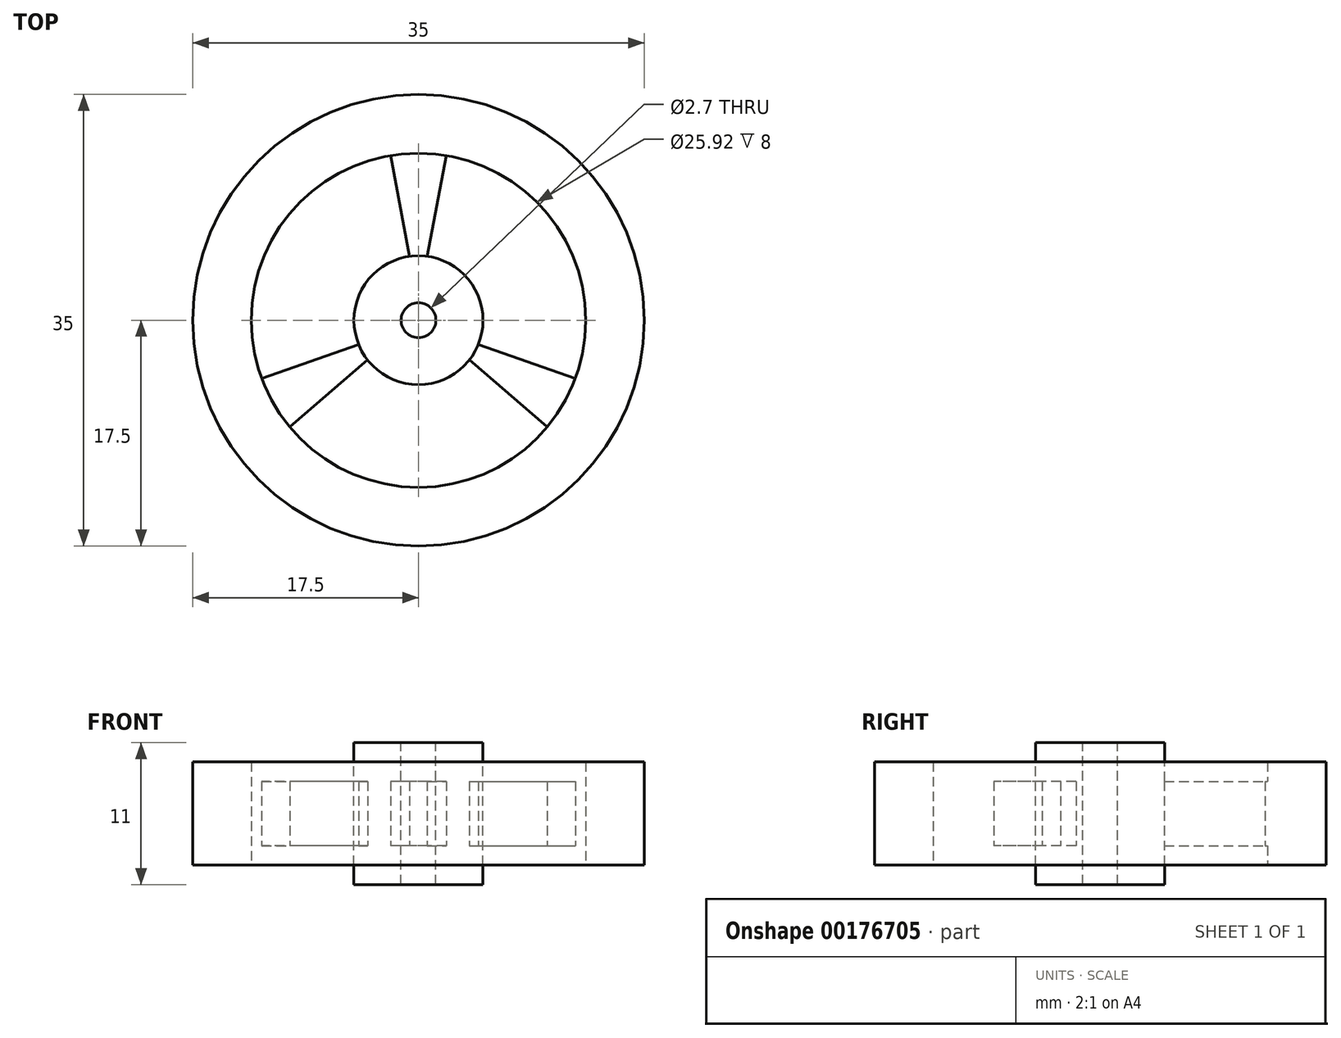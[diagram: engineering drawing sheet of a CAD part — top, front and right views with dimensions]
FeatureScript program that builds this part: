
annotation { "Feature Type Name" : "Feature", "Feature Type Description" : "" }
export const myFeature = defineFeature(function(context is Context, id is Id, definition is map)
    precondition{}
    {
        {
            var Q0;
            Q0=qCreatedBy(makeId("Top.planeOp"),FACE);
            var sketch = newSketch(context, id + "F0", { "sketchPlane" : qUnion([Q0])});
            skCircle(sketch, "E0", {"center": v(0, 0) * mm, "radius": 17.5 * mm});
            skCircle(sketch, "E1", {"center": v(0, 0) * mm, "radius": 12.96 * mm});
            skCircle(sketch, "E2", {"center": v(0, 0) * mm, "radius": 1.35 * mm});
            skLineSegment(sketch, "E3", {"start": v(0, 1.35) * mm, "end": v(0, 12.96) * mm});
            skLineSegment(sketch, "E4", {"start": v(0, 1.35) * mm, "end": v(2.17, 12.78) * mm});
            skLineSegment(sketch, "E5.MirrorCS", {"start": v(0, 1.35) * mm, "end": v(-2.17, 12.78) * mm});
            skCircle(sketch, "E6", {"center": v(0, 0) * mm, "radius": 5 * mm});
            skLineSegment(sketch, "E7.1.0", {"start": v(-1.17, -0.67) * mm, "end": v(-12.15, -4.5) * mm});
            skLineSegment(sketch, "E7.1.1", {"start": v(-1.17, -0.67) * mm, "end": v(-9.98, -8.27) * mm});
            skLineSegment(sketch, "E7.2.0", {"start": v(1.17, -0.67) * mm, "end": v(9.98, -8.27) * mm});
            skLineSegment(sketch, "E7.2.1", {"start": v(1.17, -0.68) * mm, "end": v(12.15, -4.5) * mm});
            skSolve(sketch);
        }
        {
            var Q0;
            {var subQ0=sQuery(id+"F0.wireOp",EDGE,"E5.MirrorCS");var subQ5=sQuery(id+"F0.wireOp",EDGE,"E6");var subQ6=makeQuery(id+"F0.imprint","INTERSECT",VERTEX,{"derivedFrom":[subQ0,subQ5]});Q0=makeQuery(id+"F0.imprint","IMPRINT",FACE,{"disambiguationData":[TD([[makeQuery(id+"F0.imprint","IMPRINT",EDGE,{"disambiguationData":[TD([[subQ6,-1.0]])],"derivedFrom":subQ5}),1.0]])]});}
            var Q1;
            {var subQ0=sQuery(id+"F0.wireOp",EDGE,"E7.1.0");var subQ1=sQuery(id+"F0.wireOp",EDGE,"E6");var subQ2=makeQuery(id+"F0.imprint","INTERSECT",VERTEX,{"derivedFrom":[subQ1,subQ0]});Q1=makeQuery(id+"F0.imprint","IMPRINT",FACE,{"disambiguationData":[TD([[makeQuery(id+"F0.imprint","IMPRINT",EDGE,{"disambiguationData":[TD([[subQ2,-1.0]])],"derivedFrom":subQ1}),1.0]])]});}
            var Q2;
            {var subQ0=sQuery(id+"F0.wireOp",EDGE,"E7.1.1");var subQ5=sQuery(id+"F0.wireOp",EDGE,"E6");var subQ6=makeQuery(id+"F0.imprint","INTERSECT",VERTEX,{"derivedFrom":[subQ5,subQ0]});Q2=makeQuery(id+"F0.imprint","IMPRINT",FACE,{"disambiguationData":[TD([[makeQuery(id+"F0.imprint","IMPRINT",EDGE,{"disambiguationData":[TD([[subQ6,-1.0]])],"derivedFrom":subQ5}),1.0]])]});}
            var Q3;
            {var subQ0=sQuery(id+"F0.wireOp",EDGE,"E4");var subQ5=sQuery(id+"F0.wireOp",EDGE,"E6");var subQ7=makeQuery(id+"F0.imprint","INTERSECT",VERTEX,{"derivedFrom":[subQ0,subQ5]});Q3=makeQuery(id+"F0.imprint","IMPRINT",FACE,{"disambiguationData":[TD([[makeQuery(id+"F0.imprint","IMPRINT",EDGE,{"disambiguationData":[TD([[subQ7,1.0]])],"derivedFrom":subQ5}),1.0]])]});}
            var Q4;
            {var subQ0=sQuery(id+"F0.wireOp",EDGE,"E7.2.0");var subQ1=sQuery(id+"F0.wireOp",EDGE,"E6");var subQ2=makeQuery(id+"F0.imprint","INTERSECT",VERTEX,{"derivedFrom":[subQ1,subQ0]});Q4=makeQuery(id+"F0.imprint","IMPRINT",FACE,{"disambiguationData":[TD([[makeQuery(id+"F0.imprint","IMPRINT",EDGE,{"disambiguationData":[TD([[subQ2,-1.0]])],"derivedFrom":subQ1}),1.0]])]});}
            var Q5;
            {var subQ1=sQuery(id+"F0.wireOp",EDGE,"E3");var subQ3=sQuery(id+"F0.wireOp",EDGE,"E6");var subQ4=makeQuery(id+"F0.imprint","INTERSECT",VERTEX,{"derivedFrom":[subQ1,subQ3]});Q5=makeQuery(id+"F0.imprint","IMPRINT",FACE,{"disambiguationData":[TD([[makeQuery(id+"F0.imprint","IMPRINT",EDGE,{"disambiguationData":[TD([[subQ4,1.0]])],"derivedFrom":subQ3}),1.0]])]});}
            var Q6;
            {var subQ1=sQuery(id+"F0.wireOp",EDGE,"E3");var subQ3=sQuery(id+"F0.wireOp",EDGE,"E6");var subQ4=makeQuery(id+"F0.imprint","INTERSECT",VERTEX,{"derivedFrom":[subQ1,subQ3]});Q6=makeQuery(id+"F0.imprint","IMPRINT",FACE,{"disambiguationData":[TD([[makeQuery(id+"F0.imprint","IMPRINT",EDGE,{"disambiguationData":[TD([[subQ4,-1.0]])],"derivedFrom":subQ3}),1.0]])]});}
            extrude(context, id + "F1", {"entities" : qUnion([Q0, Q1, Q2, Q3, Q4, Q5, Q6]), "endBound" : BoundingType.SYMMETRIC, "oppositeDirection" : true, "depth" : 11 * mm});
        }
        {
            var Q0;
            {var subQ0=sQuery(id+"F0.wireOp",EDGE,"E3");var subQ1=sQuery(id+"F0.wireOp",EDGE,"E1");var subQ2=makeQuery(id+"F0.imprint","INTERSECT",VERTEX,{"derivedFrom":[subQ1,subQ0]});Q0=makeQuery(id+"F0.imprint","IMPRINT",FACE,{"disambiguationData":[TD([[makeQuery(id+"F0.imprint","IMPRINT",EDGE,{"disambiguationData":[TD([[subQ2,1.0]])],"derivedFrom":subQ1}),1.0]])]});}
            var Q1;
            {var subQ0=sQuery(id+"F0.wireOp",EDGE,"E3");var subQ1=sQuery(id+"F0.wireOp",EDGE,"E1");var subQ2=makeQuery(id+"F0.imprint","INTERSECT",VERTEX,{"derivedFrom":[subQ1,subQ0]});Q1=makeQuery(id+"F0.imprint","IMPRINT",FACE,{"disambiguationData":[TD([[makeQuery(id+"F0.imprint","IMPRINT",EDGE,{"disambiguationData":[TD([[subQ2,-1.0]])],"derivedFrom":subQ1}),1.0]])]});}
            var Q2;
            {var subQ0=sQuery(id+"F0.wireOp",EDGE,"E7.1.0");var subQ1=sQuery(id+"F0.wireOp",EDGE,"E1");var subQ2=makeQuery(id+"F0.imprint","INTERSECT",VERTEX,{"derivedFrom":[subQ1,subQ0]});Q2=makeQuery(id+"F0.imprint","IMPRINT",FACE,{"disambiguationData":[TD([[makeQuery(id+"F0.imprint","IMPRINT",EDGE,{"disambiguationData":[TD([[subQ2,-1.0]])],"derivedFrom":subQ1}),1.0]])]});}
            var Q3;
            {var subQ0=sQuery(id+"F0.wireOp",EDGE,"E7.2.0");var subQ1=sQuery(id+"F0.wireOp",EDGE,"E1");var subQ2=makeQuery(id+"F0.imprint","INTERSECT",VERTEX,{"derivedFrom":[subQ1,subQ0]});Q3=makeQuery(id+"F0.imprint","IMPRINT",FACE,{"disambiguationData":[TD([[makeQuery(id+"F0.imprint","IMPRINT",EDGE,{"disambiguationData":[TD([[subQ2,-1.0]])],"derivedFrom":subQ1}),1.0]])]});}
            extrude(context, id + "F2", {"entities" : qUnion([Q0, Q1, Q2, Q3]), "operationType" : NewBodyOperationType.ADD, "endBound" : BoundingType.SYMMETRIC, "depth" : 5 * mm});
        }
        {
            var Q0;
            Q0=makeQuery(id+"F0.imprint","IMPRINT",FACE,{"disambiguationData":[TD([[makeQuery(id+"F0.imprint","IMPRINT",EDGE,{"derivedFrom":sQuery(id+"F0.wireOp",EDGE,"E0")}),1.0]])]});
            extrude(context, id + "F3", {"entities" : qUnion([Q0]), "operationType" : NewBodyOperationType.ADD, "endBound" : BoundingType.SYMMETRIC, "depth" : 8 * mm});
        }
    });
